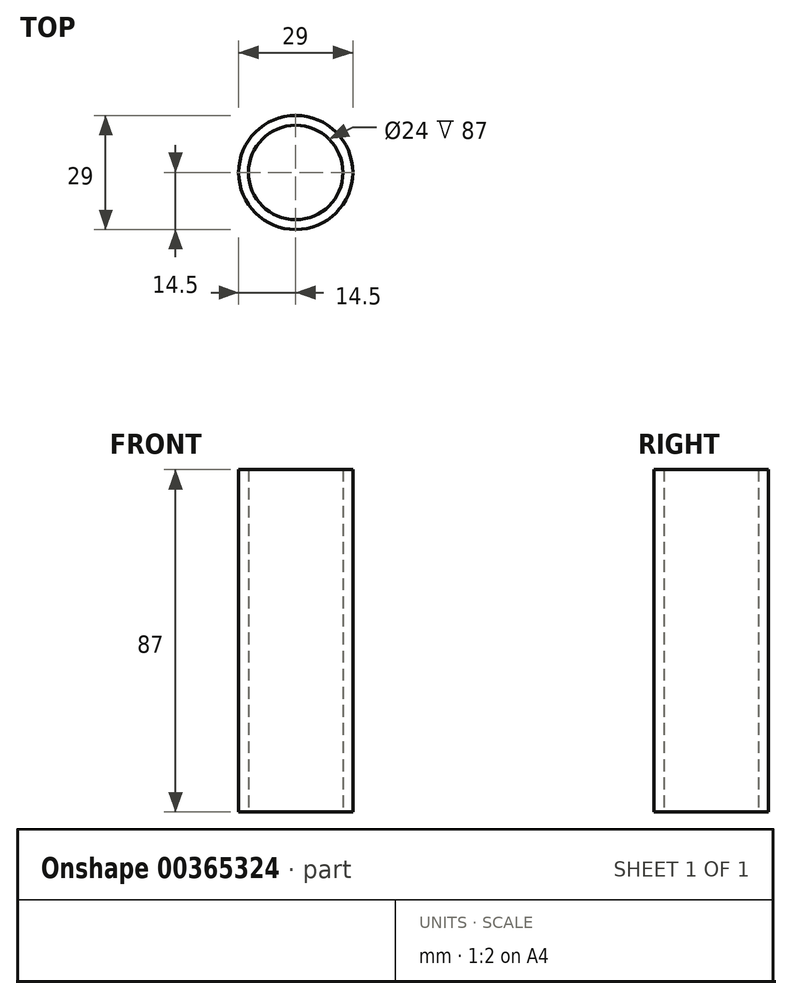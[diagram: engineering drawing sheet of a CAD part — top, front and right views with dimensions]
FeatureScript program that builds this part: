
annotation { "Feature Type Name" : "Feature", "Feature Type Description" : "" }
export const myFeature = defineFeature(function(context is Context, id is Id, definition is map)
    precondition{}
    {
        {
            var Q0;
            Q0=qCreatedBy(makeId("Top.planeOp"),FACE);
            var sketch = newSketch(context, id + "F0", { "sketchPlane" : qUnion([Q0])});
            skCircle(sketch, "E0", {"center": v(0, 0) * mm, "radius": 12 * mm});
            skCircle(sketch, "E1", {"center": v(0, 0) * mm, "radius": 14.5 * mm});
            skSolve(sketch);
        }
        {
            var Q0;
            Q0 = qSketchRegion(id + "F0", true);
            extrude(context, id + "F1", {"entities" : qUnion([Q0]), "depth" : 87 * mm});
        }
    });
